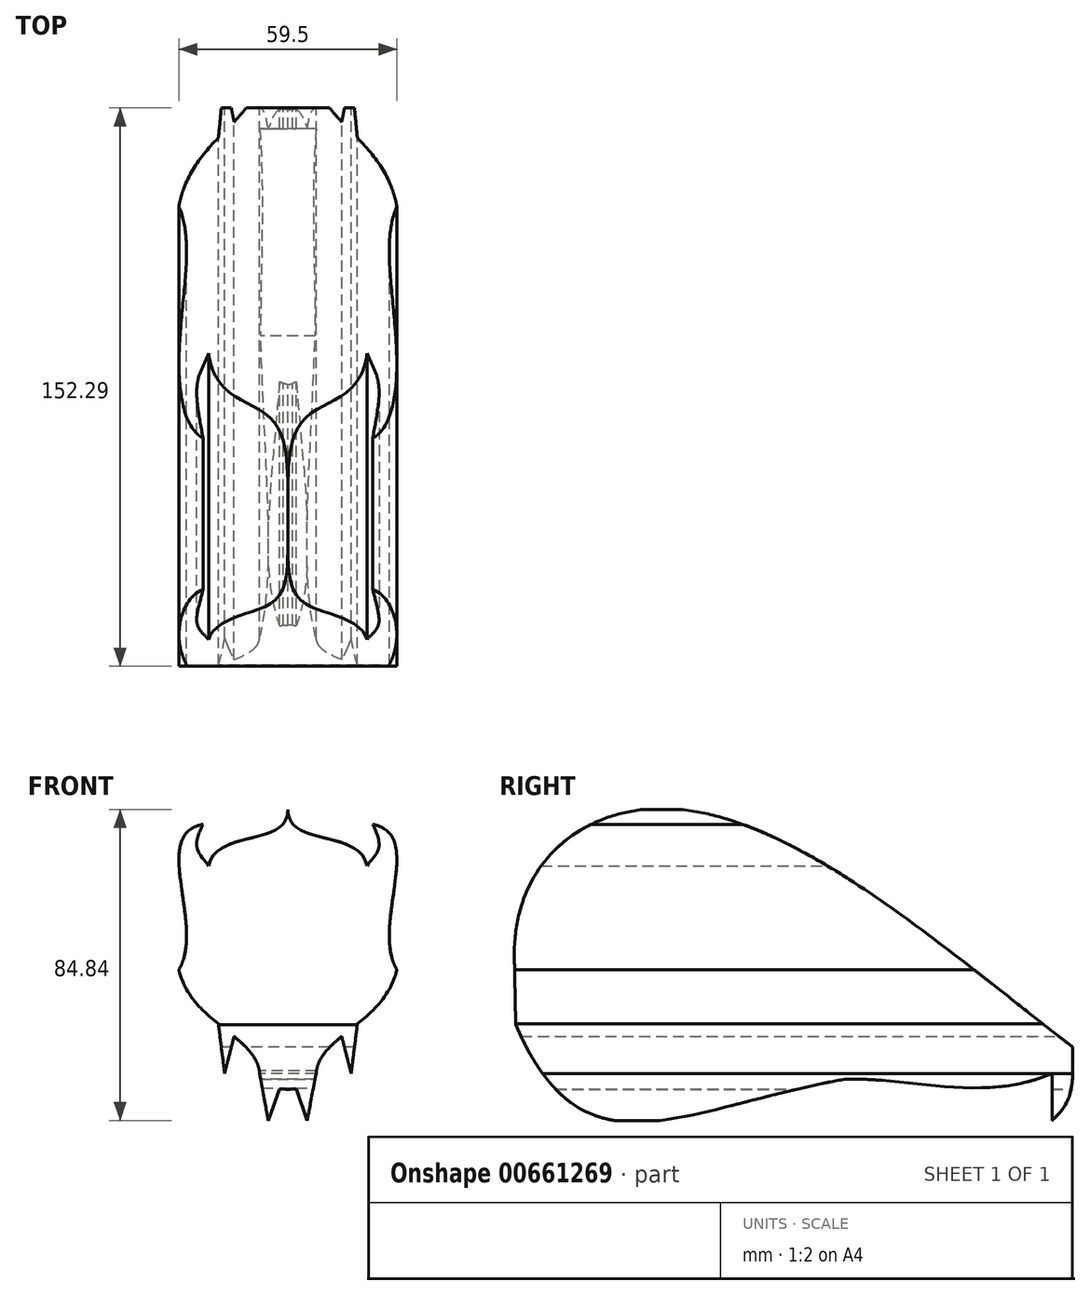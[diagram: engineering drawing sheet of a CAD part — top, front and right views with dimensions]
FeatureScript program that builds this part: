
annotation { "Feature Type Name" : "Feature", "Feature Type Description" : "" }
export const myFeature = defineFeature(function(context is Context, id is Id, definition is map)
    precondition{}
    {
        {
            var Q0;
            Q0=qCreatedBy(makeId("Front.planeOp"),FACE);
            var sketch = newSketch(context, id + "F0", { "sketchPlane" : qUnion([Q0])});
            skFitSpline(sketch, "E0", {"points": [v(0, 43.75) * mm, v(-21.6, 28.33) * mm], "startDerivative": vector(0, -31.5) * mm, "endDerivative": vector(-6.43, -30.85) * mm});
            skFitSpline(sketch, "E1", {"points": [v(-29.75, 0) * mm, v(-23.1, 39.68) * mm], "startDerivative": vector(21.85, 36.14) * mm, "endDerivative": vector(43.7, 7.71) * mm});
            skFitSpline(sketch, "E2", {"points": [v(-23.1, 39.68) * mm, v(-21.6, 28.33) * mm], "startDerivative": vector(-11.57, -21.85) * mm, "endDerivative": vector(5.78, -9.64) * mm});
            skFitSpline(sketch, "E3", {"points": [v(-29.75, 0) * mm, v(-7.7, -28.3) * mm], "startDerivative": vector(11, -44.36) * mm, "endDerivative": vector(2.16, -30.8) * mm});
            skFitSpline(sketch, "E4", {"points": [v(-7.7, -28.3) * mm, v(0, -32.62) * mm], "startDerivative": vector(5.94, -12.43) * mm, "endDerivative": vector(6.91, -0.54) * mm});
            skFitSpline(sketch, "E5.MirrorCS", {"points": [v(0, 43.75) * mm, v(21.6, 28.33) * mm], "startDerivative": vector(0, -31.5) * mm, "endDerivative": vector(6.43, -30.85) * mm});
            skFitSpline(sketch, "E6.MirrorCS", {"points": [v(23.1, 39.68) * mm, v(21.6, 28.33) * mm], "startDerivative": vector(11.57, -21.85) * mm, "endDerivative": vector(-5.78, -9.64) * mm});
            skFitSpline(sketch, "E7.MirrorCS", {"points": [v(29.75, 0) * mm, v(23.1, 39.68) * mm], "startDerivative": vector(-21.85, 36.14) * mm, "endDerivative": vector(-43.7, 7.71) * mm});
            skFitSpline(sketch, "E8.MirrorCS", {"points": [v(29.75, 0) * mm, v(7.7, -28.3) * mm], "startDerivative": vector(-11, -44.36) * mm, "endDerivative": vector(-2.16, -30.8) * mm});
            skFitSpline(sketch, "E9.MirrorCS", {"points": [v(7.7, -28.3) * mm, v(0, -32.62) * mm], "startDerivative": vector(-5.94, -12.43) * mm, "endDerivative": vector(-6.91, -0.54) * mm});
            skLineSegment(sketch, "E10", {"start": v(-7.7, -28.3) * mm, "end": v(-5.37, -41.09) * mm});
            skLineSegment(sketch, "E11", {"start": v(-5.37, -41.09) * mm, "end": v(-2.3, -32.44) * mm});
            skLineSegment(sketch, "E12", {"start": v(7.7, -28.3) * mm, "end": v(5.26, -41.09) * mm});
            skLineSegment(sketch, "E13", {"start": v(5.26, -41.09) * mm, "end": v(2.3, -32.44) * mm});
            skLineSegment(sketch, "E14", {"start": v(-18.94, -14.79) * mm, "end": v(-17.26, -28.3) * mm});
            skLineSegment(sketch, "E15", {"start": v(-17.26, -28.3) * mm, "end": v(-14.68, -18.19) * mm});
            skLineSegment(sketch, "E16.MirrorCS", {"start": v(17.26, -28.3) * mm, "end": v(14.68, -18.19) * mm});
            skLineSegment(sketch, "E17.MirrorCS", {"start": v(18.94, -14.79) * mm, "end": v(17.26, -28.3) * mm});
            skLineSegment(sketch, "E18.MirrorCS", {"start": v(-7.7, -28.3) * mm, "end": v(-5.26, -41.09) * mm});
            skLineSegment(sketch, "E19.MirrorCS", {"start": v(-5.26, -41.09) * mm, "end": v(-2.3, -32.44) * mm});
            skLineSegment(sketch, "E20.MirrorCS", {"start": v(5.37, -41.09) * mm, "end": v(2.3, -32.44) * mm});
            skLineSegment(sketch, "E21", {"start": v(-2.3, -32.44) * mm, "end": v(0, -32.62) * mm});
            skLineSegment(sketch, "E22", {"start": v(0, -32.62) * mm, "end": v(2.3, -32.44) * mm});
            skPoint(sketch, "E23.MirrorCS.end.orphan", {"position": v(20.02, 1.98) * mm});
            skPoint(sketch, "E23.MirrorCS.start.orphan", {"position": v(11.32, 12.5) * mm});
            skPoint(sketch, "E24.start.orphan", {"position": v(0, 27.87) * mm});
            skPoint(sketch, "E25.MirrorCS.end.orphan", {"position": v(2.6, 19.85) * mm});
            skPoint(sketch, "E26.MirrorCS.end.orphan", {"position": v(2.6, 2.73) * mm});
            skPoint(sketch, "E27.start.orphan", {"position": v(-2.6, 19.85) * mm});
            skPoint(sketch, "E28.start.orphan", {"position": v(-2.6, 2.73) * mm});
            skPoint(sketch, "E29.start.orphan", {"position": v(-2.6, -14.09) * mm});
            skPoint(sketch, "E30.end.orphan", {"position": v(2.6, -14.09) * mm});
            skPoint(sketch, "E31.MirrorCS.end.orphan", {"position": v(6.84, -15.9) * mm});
            skPoint(sketch, "E31.MirrorCS.start.orphan", {"position": v(4.33, -13.53) * mm});
            skPoint(sketch, "E32.MirrorCS.end.orphan", {"position": v(2.6, -23.33) * mm});
            skPoint(sketch, "E33.MirrorCS.end.orphan", {"position": v(0, -19.7) * mm});
            skPoint(sketch, "E34.end.orphan", {"position": v(-2.6, -23.33) * mm});
            skPoint(sketch, "E35.end.orphan", {"position": v(-6.84, -15.9) * mm});
            skPoint(sketch, "E35.start.orphan", {"position": v(-4.33, -13.53) * mm});
            skPoint(sketch, "E36.1.internal.orphan", {"position": v(-7, 0) * mm});
            skPoint(sketch, "E37.end.orphan", {"position": v(-20.02, 1.98) * mm});
            skPoint(sketch, "E37.start.orphan", {"position": v(-11.32, 12.5) * mm});
            skSolve(sketch);
        }
        {
            var Q0;
            Q0 = qSketchRegion(id + "F0", true);
            extrude(context, id + "F1", {"entities" : qUnion([Q0]), "depth" : 152.4 * mm, "offsetDistance" : 25.4 * mm});
        }
        {
            var Q0;
            Q0=qCreatedBy(makeId("Right.planeOp"),FACE);
            var sketch = newSketch(context, id + "F2", { "sketchPlane" : qUnion([Q0])});
            skFitSpline(sketch, "E38", {"points": [v(-152.28, 3.47) * mm, v(-110.32, 43.96) * mm, v(0, -21.12) * mm], "startDerivative": vector(-2.75, 196.85) * mm, "endDerivative": vector(185.49, -143.33) * mm});
            skFitSpline(sketch, "E39", {"points": [v(0, -21.12) * mm, v(-5.68, -41.09) * mm], "startDerivative": vector(0, -29.95) * mm, "endDerivative": vector(-18.86, -16.64) * mm});
            skLineSegment(sketch, "E40", {"start": v(-5.68, -41.09) * mm, "end": v(-5.68, -28.33) * mm});
            skFitSpline(sketch, "E41", {"points": [v(-26.57, -28.33) * mm, v(-119.38, -41.54) * mm, v(-151.91, -14.92) * mm], "startDerivative": vector(-181.5, 22.73) * mm, "endDerivative": vector(-59.46, 138.28) * mm});
            skFitSpline(sketch, "E42", {"points": [v(-62.2, -29.83) * mm, v(-5.68, -28.33) * mm], "startDerivative": vector(56.52, 1.51) * mm, "endDerivative": vector(57.13, 24.1) * mm});
            skLineSegment(sketch, "E43", {"start": v(-151.91, -14.92) * mm, "end": v(-152.28, 3.47) * mm});
            skLineSegment(sketch, "E44", {"start": v(0, -21.12) * mm, "end": v(0, -31.1) * mm});
            skLineSegment(sketch, "E45", {"start": v(-151.91, 49.75) * mm, "end": v(0, 49.75) * mm});
            skLineSegment(sketch, "E46", {"start": v(0, 49.75) * mm, "end": v(8.37, 49.75) * mm});
            skLineSegment(sketch, "E47", {"start": v(8.37, 49.75) * mm, "end": v(8.37, -47.13) * mm});
            skLineSegment(sketch, "E48", {"start": v(8.37, -47.13) * mm, "end": v(-155.61, -47.13) * mm});
            skLineSegment(sketch, "E49", {"start": v(-155.61, -47.13) * mm, "end": v(-155.61, 49.75) * mm});
            skLineSegment(sketch, "E50", {"start": v(-155.61, 49.75) * mm, "end": v(-151.91, 49.75) * mm});
            skFitSpline(sketch, "E51", {"points": [v(-22.02, -3.83) * mm, v(-59.77, 23.88) * mm], "startDerivative": vector(-38.05, 27.22) * mm, "endDerivative": vector(-8.84, 57.13) * mm});
            skFitSpline(sketch, "E52.trimOffspring", {"points": [v(-152.28, 3.47) * mm, v(-110.32, 43.96) * mm, v(0, -21.12) * mm], "startDerivative": vector(-2.75, 196.85) * mm, "endDerivative": vector(185.49, -143.33) * mm});
            skFitSpline(sketch, "E53", {"points": [v(-73.64, 32.18) * mm, v(-106.25, 34.16) * mm, v(-116.41, 43.78) * mm, v(-130.65, 30.1) * mm, v(-149.7, 19.42) * mm], "startDerivative": vector(-123.92, -14.94) * mm, "endDerivative": vector(-78.56, -29.56) * mm});
            skFitSpline(sketch, "E54.trimOffspring", {"points": [v(-152.28, 3.47) * mm, v(-110.32, 43.96) * mm, v(0, -21.12) * mm], "startDerivative": vector(-2.75, 196.85) * mm, "endDerivative": vector(185.49, -143.33) * mm});
            skLineSegment(sketch, "E55", {"start": v(-62.2, -29.83) * mm, "end": v(-146.72, -25.1) * mm});
            skSolve(sketch);
        }
        {
            var Q0;
            Q0 = qSketchRegion(id + "F2", true);
            extrude(context, id + "F3", {"entities" : qUnion([Q0]), "operationType" : NewBodyOperationType.REMOVE, "endBound" : BoundingType.SYMMETRIC, "depth" : 127 * mm, "offsetDistance" : 25.4 * mm});
        }
    });
